# Revit family: Воздухонагреватель водяной для прямоугольных каналов W
name_source: partatom
category: Оборудование
units: mm (PartAtom-declared; Revit-internal decimal feet)

## family parameters
Всегда вертикально = Да
Заголовок OmniClass = Climate Control (HVAC)
На основе рабочей плоскости = Нет
Номер OmniClass = 23.75.00.00
Общий = Нет
При загрузке вырезать с полостями = Нет
Размер круглого соединителя = Использовать диаметр
Тип детали = Нормальный
Точка расчета площади = Нет

## types (16) — shared parameters
ADSK_Единица измерения = шт.
ADSK_Завод-изготовитель = Naveka
ADSK_Наименование = Воздухонагреватель водяной для прямоугольного канала
L = 150 мм
w = 43 мм
Материал = RAL 0000 Серый металл
Материал 2 = Материал 2

## per-type parameters (varying)
| type | ADSK_Масса_Текст | B | B1 | H | h |
| W2-4020 | 4.8 кг | 400 мм | 494 мм | 200 мм | 185 мм |
| W2-10050 | 4.8 кг | 1000 мм | 1114 мм | 500 мм | 485 мм |
| W2-5025 | 6.2 кг | 500 мм | 594 мм | 250 мм | 235 мм |
| W2-5030 | 6.9 кг | 500 мм | 594 мм | 300 мм | 285 мм |
| W2-6030 | 7.6 кг | 600 мм | 694 мм | 300 мм | 285 мм |
| W2-6035 | 8.6 кг | 600 мм | 694 мм | 350 мм | 335 мм |
| W2-7040 | 10.3 кг | 700 мм | 794 мм | 400 мм | 385 мм |
| W2-8050 | 13.0 кг | 800 мм | 894 мм | 500 мм | 485 мм |
| W3-8050 | 16.4 кг | 800 мм | 894 мм | 500 мм | 485 мм |
| W3-7040 | 12.7 кг | 700 мм | 794 мм | 400 мм | 385 мм |
| W3-10050 | 19.81 кг | 1000 мм | 1114 мм | 500 мм | 485 мм |
| W3-4020 | 5.54 кг | 400 мм | 494 мм | 200 мм | 185 мм |
| W3-5025 | 7.5 кг | 500 мм | 594 мм | 250 мм | 235 мм |
| W3-5030 | 8.42 кг | 500 мм | 594 мм | 300 мм | 285 мм |
| W3-6030 | 9.42 кг | 600 мм | 694 мм | 300 мм | 285 мм |
| W3-6035 | 10.5 кг | 600 мм | 694 мм | 350 мм | 335 мм |

note: column(s) folded — value = type name in every type: ADSK_Марка
